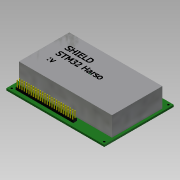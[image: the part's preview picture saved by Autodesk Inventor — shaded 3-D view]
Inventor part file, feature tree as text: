
AUTODESK INVENTOR PART (.ipt)
format: ipt  version: 2015 SP1 (Build 190203100, 203)  size: 1,310,720 bytes
history: native  units: mm
features: extrude x6, sketch x5, projected_geometry x2, pattern_linear x1, mirror x1
ambient origin geometry x8: Origin, YZ Plane, XZ Plane, XY Plane, X Axis, Y Axis, Z Axis, Center Point
bodies: Body1 (feature_tree)
feature tree (15):
  sketch  "Sketch1"  dims[d0=107.193mm d1=75.991mm]
  extrude  "Extrusion2"  Depth=75.991mm
  extrude  "Extrusion3"  Depth=2.0mm
  pattern_linear  "Rectangular Pattern1"  Spacing1=3.0mm  [1 undecoded]
  extrude  "Extrusion4"  Depth=21.26mm
  mirror  "Mirror1"
  extrude  "Extrusion5"  Depth=21.26mm
  extrude  "Extrusion6"  Depth=21.26mm
  extrude  "Extrusion7"  Depth=21.26mm
  sketch  "Sketch5"  dims[d6=3.0mm d7=3.0mm d8=3.0mm d9=3.0mm d10=3.0mm d11=3.0mm d12=3.0mm d13=3.0mm d16=0.793mm d17=0.784mm d18=4.808mm d19=1.455mm d20=250.0mm d22=2.52mm d23=20.0mm d25=2.5mm d28=0.784mm d29=4.415mm d30=250.0mm d32=2.52mm d33=20.0mm d35=2.5mm d38=1.27mm d39=1.27mm d40=1.27mm d41=1.27mm d42=2.0mm d43=0.0mm d44=11.5mm d45=0.0mm d46=250.0mm d48=2.52mm d49=20.0mm d51=2.5mm d52=7.0mm d53=0.0mm d54=2.0mm d55=0.0mm d56=63.0mm d57=4.0mm d58=0.836mm d59=0.358mm d61=2.5mm d62=0.0mm d65=21.26mm d66=0.0mm]
  sketch  "Sketch2"  dims[d2=2.0mm d3=2.0mm]
  sketch  "Sketch3"  dims[d4=2.0mm]
  projected_geometry  "Projected Loop1"
  projected_geometry  "Projected Loop2"
  sketch  "Sketch4"  dims[d5=2.0mm]
note: 1 required parameter value undecoded (feature->parameter linkage not recoverable at this tier; creation-order binding heuristic only, values carry confidence <= 0.55)
